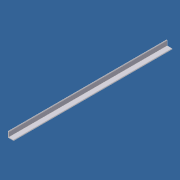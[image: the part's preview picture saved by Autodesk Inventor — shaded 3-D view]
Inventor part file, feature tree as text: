
AUTODESK INVENTOR PART (.ipt)
format: ipt  version: unknown  size: 160,256 bytes
history: native  units: in
note: dims shown in document units (in); Inventor stores cm internally (conversion verified against a paired STEP export)
features: extrude x1, sketch x1
ambient origin geometry x8: Origin, YZ Plane, XZ Plane, XY Plane, X Axis, Y Axis, Z Axis, Center Point
feature tree (2):
  extrude  "Extrusion1"  Depth=1.5in
  sketch  "Sketch1"  dims[d0=1.5in d1=1.5in d2=0.125in d3=0.125in d4=43.25in d5=0.0in d6=0.125in]
